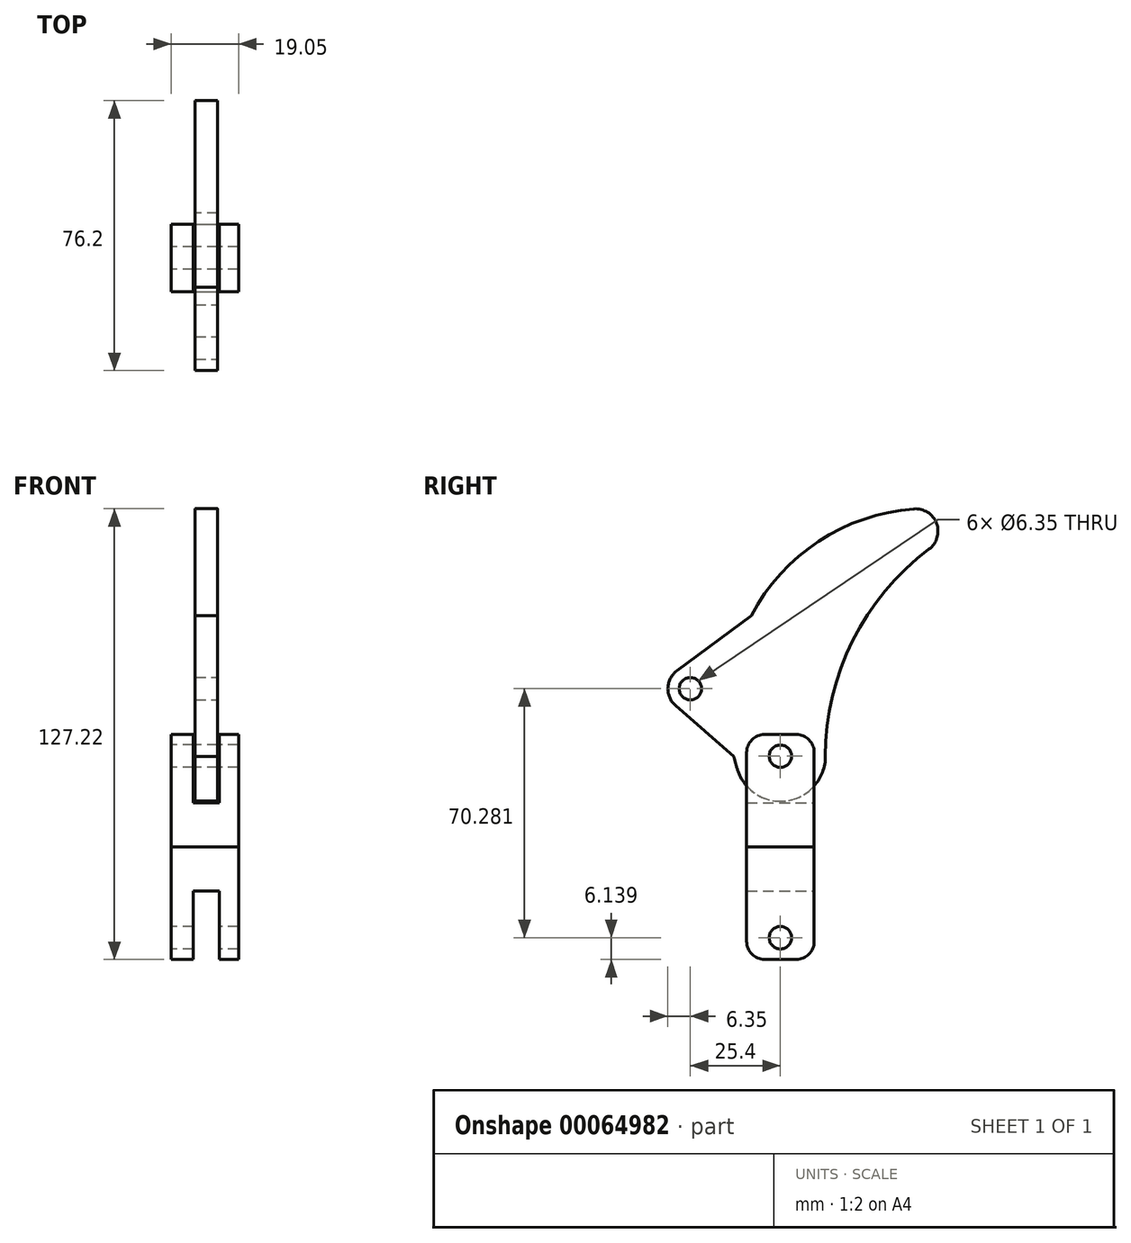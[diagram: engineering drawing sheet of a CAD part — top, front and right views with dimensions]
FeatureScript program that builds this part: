
annotation { "Feature Type Name" : "Feature", "Feature Type Description" : "" }
export const myFeature = defineFeature(function(context is Context, id is Id, definition is map)
    precondition{}
    {
        {
            var Q0;
            Q0=qCreatedBy(makeId("Right.planeOp"),FACE);
            var sketch = newSketch(context, id + "F0", { "sketchPlane" : qUnion([Q0])});
            skLineSegment(sketch, "E0.bottom", {"start": v(-76.2, 76.2) * mm, "end": v(76.2, 76.2) * mm});
            skLineSegment(sketch, "E0.top", {"start": v(-76.2, -76.2) * mm, "end": v(76.2, -76.2) * mm});
            skLineSegment(sketch, "E0.left", {"start": v(-76.2, 76.2) * mm, "end": v(-76.2, -76.2) * mm});
            skLineSegment(sketch, "E0.right", {"start": v(76.2, 76.2) * mm, "end": v(76.2, -76.2) * mm});
            skArc(sketch, "E1", {"start": v(-12.1, -3.83) * mm, "mid": v(1.94, -12.55) * mm, "end": v(12.7, 0) * mm});
            skCircle(sketch, "E2", {"center": v(0, 0) * mm, "radius": 3.18 * mm});
            skArc(sketch, "E3", {"start": v(41.9, 58.42) * mm, "mid": v(44.04, 65.74) * mm, "end": v(37.61, 69.83) * mm});
            skArc(sketch, "E4", {"start": v(37.61, 69.83) * mm, "mid": v(-5.05, 45.01) * mm, "end": v(-12.1, -3.83) * mm});
            skArc(sketch, "E5", {"start": v(41.9, 58.42) * mm, "mid": v(20.4, 32.66) * mm, "end": v(12.7, 0) * mm});
            skSolve(sketch);
        }
        {
            var Q0;
            Q0=makeQuery(id+"F0.imprint","IMPRINT",FACE,{"disambiguationData":[TD([[makeQuery(id+"F0.imprint","IMPRINT",EDGE,{"derivedFrom":sQuery(id+"F0.wireOp",EDGE,"E1")}),1.0]])]});
            extrude(context, id + "F1", {"entities" : qUnion([Q0]), "depth" : 6.35 * mm});
        }
        {
            var Q0;
            Q0=makeQuery(id+"F1.opExtrude","CAP_FACE",FACE,{"disambiguationData":[OSD([sQuery(id+"F0.wireOp",EDGE,"E1"),sQuery(id+"F0.wireOp",EDGE,"E2"),sQuery(id+"F0.wireOp",EDGE,"E3"),sQuery(id+"F0.wireOp",EDGE,"E4"),sQuery(id+"F0.wireOp",EDGE,"E5")])],"isStart":false});
            var sketch = newSketch(context, id + "F2", { "sketchPlane" : qUnion([Q0])});
            skCircle(sketch, "E6", {"center": v(-25.4, 19.05) * mm, "radius": 3.18 * mm});
            skArc(sketch, "E7", {"start": v(-29.18, 24.15) * mm, "mid": v(-31.75, 19.3) * mm, "end": v(-29.57, 14.26) * mm});
            skArc(sketch, "E8.0", {"start": v(37.61, 69.83) * mm, "mid": v(-5.05, 45.01) * mm, "end": v(-12.1, -3.83) * mm});
            skLineSegment(sketch, "E9", {"start": v(-29.18, 24.15) * mm, "end": v(-8.24, 39.67) * mm});
            skLineSegment(sketch, "E10", {"start": v(-29.57, 14.26) * mm, "end": v(-13.17, -0.03) * mm});
            skSolve(sketch);
        }
        {
            var Q0;
            Q0=makeQuery(id+"F2.imprint","IMPRINT",FACE,{"disambiguationData":[TD([[makeQuery(id+"F2.imprint","IMPRINT",EDGE,{"derivedFrom":sQuery(id+"F2.wireOp",EDGE,"E6")}),-1.0]])]});
            extrude(context, id + "F3", {"entities" : qUnion([Q0]), "operationType" : NewBodyOperationType.ADD, "oppositeDirection" : true, "depth" : 6.35 * mm});
        }
        {
            var Q0;
            Q0=qCreatedBy(makeId("Front.planeOp"),FACE);
            var sketch = newSketch(context, id + "F4", { "sketchPlane" : qUnion([Q0])});
            skLineSegment(sketch, "E11.bottom", {"start": v(-6.76, 6.13) * mm, "end": v(0, 6.13) * mm});
            skLineSegment(sketch, "E11.top", {"start": v(-6.76, -25.62) * mm, "end": v(12.3, -25.62) * mm});
            skLineSegment(sketch, "E11.left", {"start": v(-6.76, 6.13) * mm, "end": v(-6.76, -25.62) * mm});
            skLineSegment(sketch, "E11.right", {"start": v(12.3, 6.13) * mm, "end": v(12.3, -25.62) * mm});
            skLineSegment(sketch, "E12.0.0", {"start": v(6.35, -0.03) * mm, "end": v(6.35, 6.13) * mm});
            skLineSegment(sketch, "E12.0.1", {"start": v(6.35, 14.26) * mm, "end": v(0, 14.26) * mm});
            skLineSegment(sketch, "E12.0.2", {"start": v(0, 6.13) * mm, "end": v(0, -0.03) * mm});
            skLineSegment(sketch, "E12.1.1", {"start": v(0, -0.03) * mm, "end": v(0, -3.83) * mm});
            skLineSegment(sketch, "E12.1.3", {"start": v(6.35, -3.83) * mm, "end": v(6.35, -0.03) * mm});
            skLineSegment(sketch, "E12.2.0", {"start": v(0, -0.03) * mm, "end": v(0, -12.7) * mm});
            skLineSegment(sketch, "E12.2.2", {"start": v(6.35, -12.7) * mm, "end": v(6.35, 0) * mm});
            skLineSegment(sketch, "E13.trimOffspring", {"start": v(6.35, 6.13) * mm, "end": v(12.3, 6.13) * mm});
            skLineSegment(sketch, "E14", {"start": v(0, -12.7) * mm, "end": v(6.35, -12.7) * mm});
            skPoint(sketch, "E15.orphan", {"position": v(0, 0) * mm});
            skLineSegment(sketch, "E16", {"start": v(0, 6.13) * mm, "end": v(0, -12.7) * mm});
            skLineSegment(sketch, "E17", {"start": v(6.35, -12.7) * mm, "end": v(6.35, 6.13) * mm});
            skLineSegment(sketch, "E18.0", {"start": v(6.86, -13.2) * mm, "end": v(6.86, 6.13) * mm});
            skLineSegment(sketch, "E18.1", {"start": v(-0.5, -13.2) * mm, "end": v(6.86, -13.2) * mm});
            skLineSegment(sketch, "E18.2", {"start": v(-0.5, 6.13) * mm, "end": v(-0.5, -13.2) * mm});
            skSolve(sketch);
        }
        {
            var Q0;
            Q0=makeQuery(id+"F4.imprint","IMPRINT",FACE,{"disambiguationData":[TD([[makeQuery(id+"F4.imprint","IMPRINT",EDGE,{"derivedFrom":sQuery(id+"F4.wireOp",EDGE,"E11.top")}),1.0]])]});
            extrude(context, id + "F5", {"entities" : qUnion([Q0]), "depth" : 19.05 * mm, "symmetric" : true});
        }
        {
            var Q0;
            Q0=makeQuery(id+"F5.opExtrude","SWEPT_FACE",FACE,{"disambiguationData":[OSD([sQuery(id+"F4.wireOp",EDGE,"E11.left")])]});
            var sketch = newSketch(context, id + "F6", { "sketchPlane" : qUnion([Q0])});
            skCircle(sketch, "E19.0", {"center": v(0, 0) * mm, "radius": 3.18 * mm});
            skSolve(sketch);
        }
        {
            var Q0;
            Q0=makeQuery(id+"F6.imprint","IMPRINT",FACE,{"disambiguationData":[TD([[makeQuery(id+"F6.imprint","IMPRINT",EDGE,{"derivedFrom":sQuery(id+"F6.wireOp",EDGE,"E19.0")}),1.0]])]});
            extrude(context, id + "F7", {"entities" : qUnion([Q0]), "operationType" : NewBodyOperationType.REMOVE, "oppositeDirection" : true, "depth" : 25.4 * mm});
        }
        {
            var Q0;
            Q0=makeQuery(id+"F5.opExtrude","CAP_EDGE",EDGE,{"disambiguationData":[OSD([sQuery(id+"F4.wireOp",EDGE,"E11.bottom")])],"isStart":false});
            var Q1;
            Q1=makeQuery(id+"F5.opExtrude","CAP_EDGE",EDGE,{"disambiguationData":[OSD([sQuery(id+"F4.wireOp",EDGE,"E11.bottom")])],"isStart":true});
            var Q2;
            Q2=makeQuery(id+"F5.opExtrude","CAP_EDGE",EDGE,{"disambiguationData":[OSD([sQuery(id+"F4.wireOp",EDGE,"E13.trimOffspring")])],"isStart":false});
            var Q3;
            Q3=makeQuery(id+"F5.opExtrude","CAP_EDGE",EDGE,{"disambiguationData":[OSD([sQuery(id+"F4.wireOp",EDGE,"E13.trimOffspring")])],"isStart":true});
            fillet(context, id + "F8", {"entities" : qUnion([Q0, Q1, Q2, Q3]), "radius" : 5.08 * mm, "tangentPropagation" : true, "allowEdgeOverflow" : false});
        }
        {
            var Q0;
            Q0=makeQuery(id+"F5.opExtrude","SWEPT_BODY",BODY,{"disambiguationData":[OSD([sQuery(id+"F4.wireOp",EDGE,"E11.bottom"),sQuery(id+"F4.wireOp",EDGE,"E11.top"),sQuery(id+"F4.wireOp",EDGE,"E11.left"),sQuery(id+"F4.wireOp",EDGE,"E11.right"),sQuery(id+"F4.wireOp",EDGE,"E13.trimOffspring"),sQuery(id+"F4.wireOp",EDGE,"E18.0"),sQuery(id+"F4.wireOp",EDGE,"E18.1"),sQuery(id+"F4.wireOp",EDGE,"E18.2")])]});
            var Q1;
            Q1=makeQuery(id+"F5.opExtrude","SWEPT_FACE",FACE,{"disambiguationData":[OSD([sQuery(id+"F4.wireOp",EDGE,"E11.top")])]});
            mirror(context, id + "F9", {"operationType" : NewBodyOperationType.ADD, "entities" : qUnion([Q0]), "mirrorPlane" : qUnion([Q1])});
        }
    });
